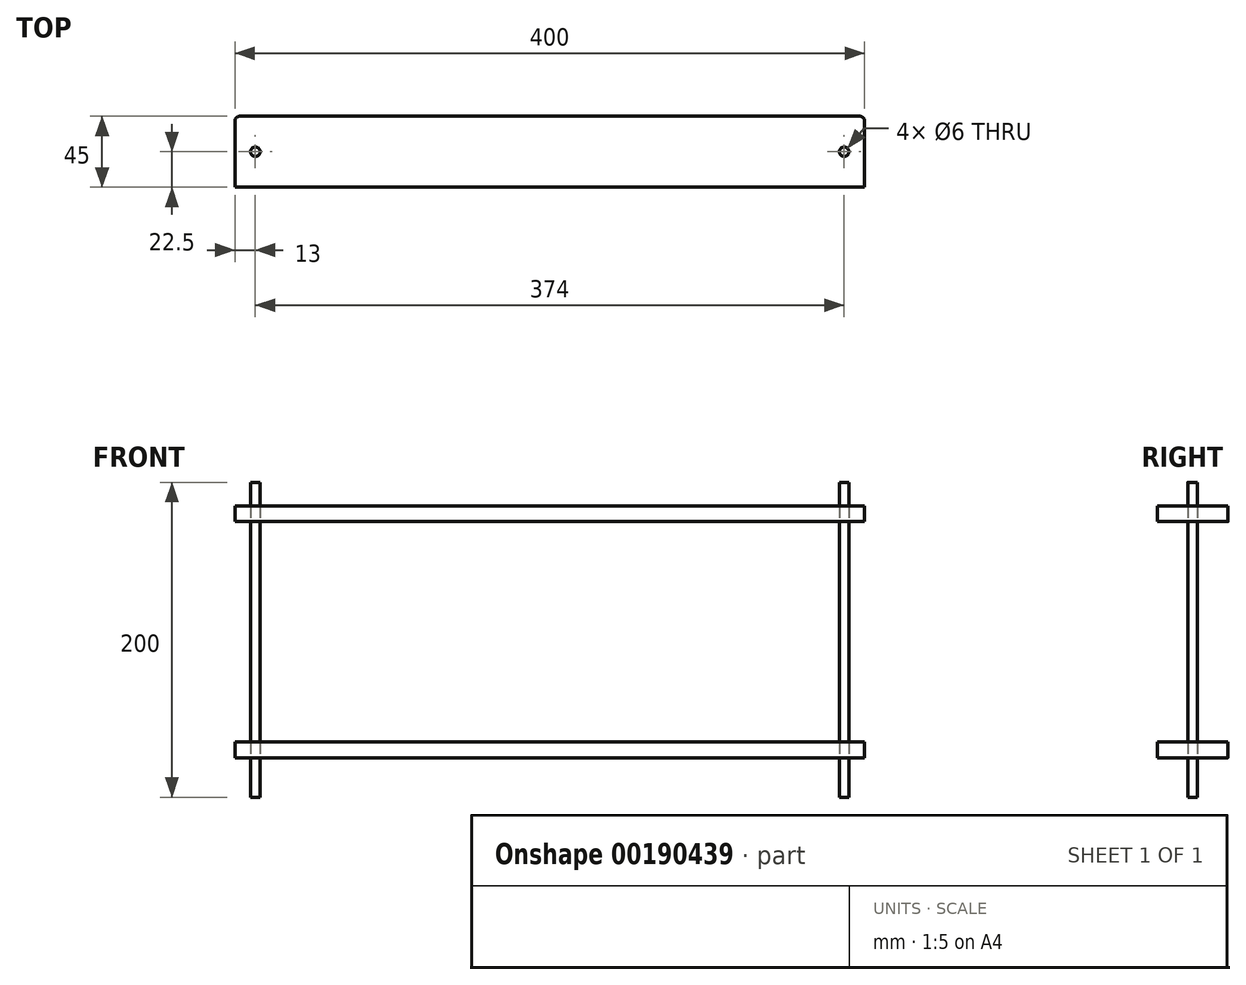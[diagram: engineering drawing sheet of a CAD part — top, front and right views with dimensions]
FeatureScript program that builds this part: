
annotation { "Feature Type Name" : "Feature", "Feature Type Description" : "" }
export const myFeature = defineFeature(function(context is Context, id is Id, definition is map)
    precondition{}
    {
        {
            var Q0;
            Q0=qCreatedBy(makeId("Top.planeOp"),FACE);
            var sketch = newSketch(context, id + "F0", { "sketchPlane" : qUnion([Q0])});
            skLineSegment(sketch, "E0.bottom", {"start": v(30, 30) * mm, "end": v(430, 30) * mm});
            skLineSegment(sketch, "E0.top", {"start": v(33, 75) * mm, "end": v(427, 75) * mm});
            skLineSegment(sketch, "E0.left", {"start": v(30, 30) * mm, "end": v(30, 72) * mm});
            skLineSegment(sketch, "E0.right", {"start": v(430, 30) * mm, "end": v(430, 72) * mm});
            skCircle(sketch, "E1", {"center": v(43, 52.5) * mm, "radius": 3 * mm});
            skPoint(sketch, "E1.centerSnap0", {"position": v(30, 52.5) * mm});
            skCircle(sketch, "E2", {"center": v(417, 52.5) * mm, "radius": 3 * mm});
            skPoint(sketch, "E3.visualSharp", {"position": v(30, 75) * mm});
            skArc(sketch, "E3.filletArc", {"start": v(33, 75) * mm, "mid": v(30.88, 74.12) * mm, "end": v(30, 72) * mm});
            skPoint(sketch, "E4.visualSharp", {"position": v(430, 75) * mm});
            skArc(sketch, "E4.filletArc", {"start": v(430, 72) * mm, "mid": v(429.12, 74.12) * mm, "end": v(427, 75) * mm});
            skSolve(sketch);
        }
        {
            var Q0;
            Q0 = qSketchRegion(id + "F0", true);
            var Q1;
            Q1=makeQuery(id+"F0.imprint","IMPRINT",FACE,{"disambiguationData":[TD([[makeQuery(id+"F0.imprint","IMPRINT",EDGE,{"derivedFrom":sQuery(id+"F0.wireOp",EDGE,"E0.bottom")}),1.0]])]});
            extrude(context, id + "F1", {"entities" : qUnion([Q0, Q1]), "depth" : 10 * mm});
        }
        {
            var Q0;
            Q0=makeQuery(id+"F1.opExtrude","SWEPT_BODY",BODY,{"disambiguationData":[OSD([sQuery(id+"F0.wireOp",EDGE,"E0.bottom"),sQuery(id+"F0.wireOp",EDGE,"E0.top"),sQuery(id+"F0.wireOp",EDGE,"E0.left"),sQuery(id+"F0.wireOp",EDGE,"E0.right"),sQuery(id+"F0.wireOp",EDGE,"E1"),sQuery(id+"F0.wireOp",EDGE,"E2"),sQuery(id+"F0.wireOp",EDGE,"E3.filletArc"),sQuery(id+"F0.wireOp",EDGE,"E4.filletArc")])]});
            transform(context, id + "F2", {"entities" : qUnion([Q0]), "transformType" : TransformType.TRANSLATION_3D, "dx" : 0 * mm, "dy" : 0 * mm, "dz" : 150 * mm, "makeCopy" : true});
        }
        {
            var Q0;
            Q0=makeQuery(id+"F0.imprint","IMPRINT",FACE,{"disambiguationData":[TD([[makeQuery(id+"F0.imprint","IMPRINT",EDGE,{"derivedFrom":sQuery(id+"F0.wireOp",EDGE,"E2")}),1.0]])]});
            var Q1;
            Q1=makeQuery(id+"F0.imprint","IMPRINT",FACE,{"disambiguationData":[TD([[makeQuery(id+"F0.imprint","IMPRINT",EDGE,{"derivedFrom":sQuery(id+"F0.wireOp",EDGE,"E1")}),1.0]])]});
            extrude(context, id + "F3", {"entities" : qUnion([Q0, Q1]), "depth" : 175 * mm, "hasSecondDirection" : true, "secondDirectionOppositeDirection" : true, "secondDirectionDepth" : 25 * mm});
        }
    });
